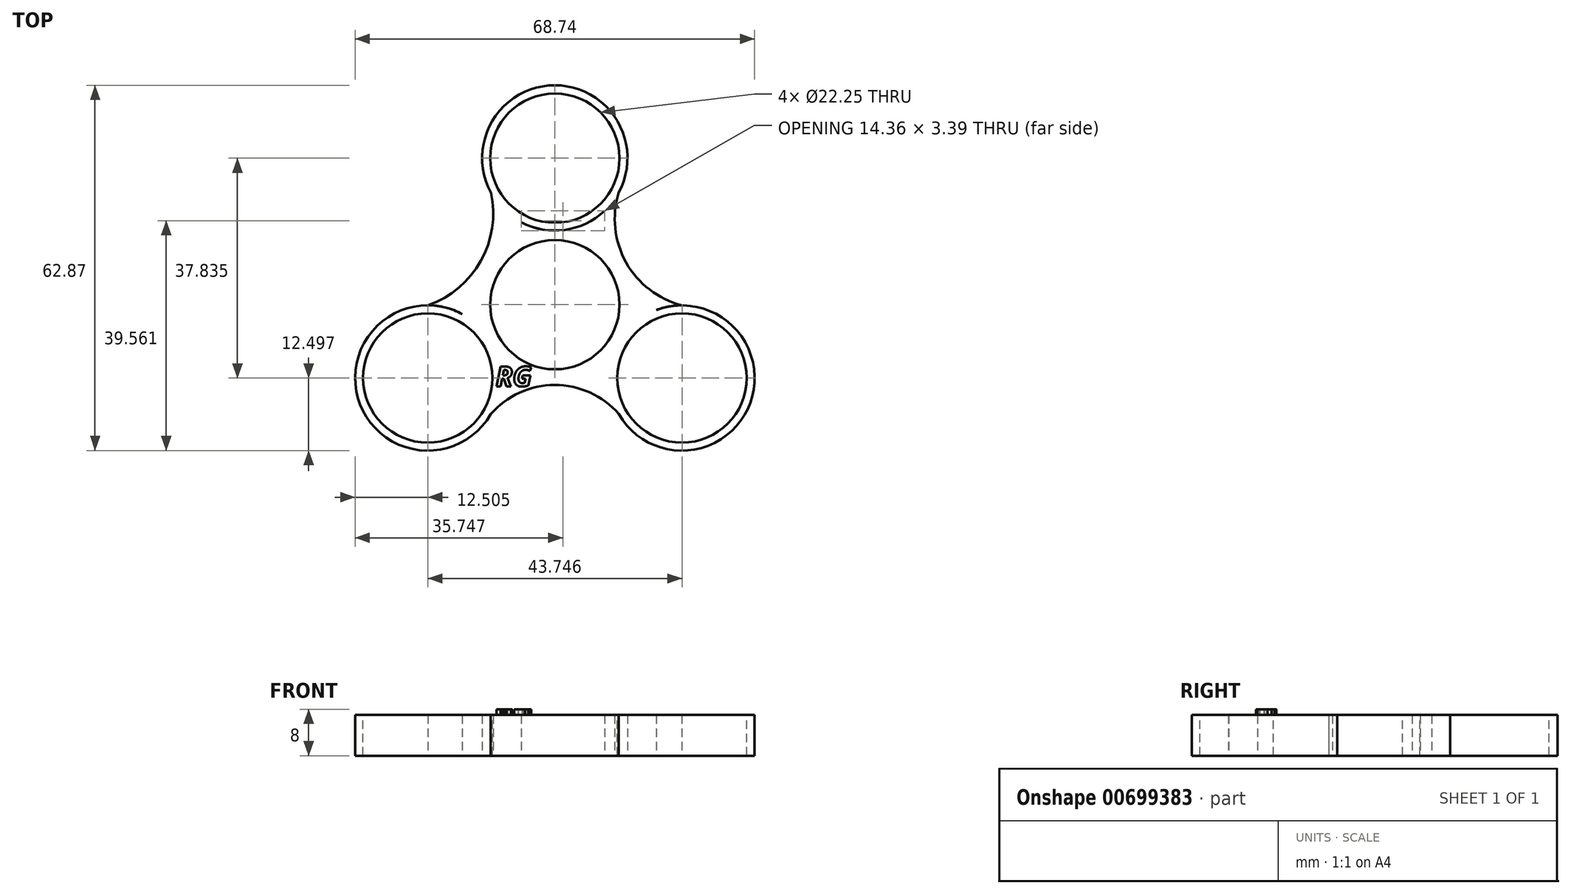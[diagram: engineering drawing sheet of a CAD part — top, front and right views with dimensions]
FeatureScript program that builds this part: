
annotation { "Feature Type Name" : "Feature", "Feature Type Description" : "" }
export const myFeature = defineFeature(function(context is Context, id is Id, definition is map)
    precondition{}
    {
        {
            var Q0;
            Q0=qCreatedBy(makeId("Top.planeOp"),FACE);
            var sketch = newSketch(context, id + "F0", { "sketchPlane" : qUnion([Q0])});
            skCircle(sketch, "E0", {"center": v(0, 0) * mm, "radius": 11.12 * mm});
            skCircle(sketch, "E1", {"center": v(0, 25.25) * mm, "radius": 11.12 * mm});
            skCircle(sketch, "E2", {"center": v(-21.87, -12.62) * mm, "radius": 11.12 * mm});
            skCircle(sketch, "E3", {"center": v(21.87, -12.62) * mm, "radius": 11.12 * mm});
            skSolve(sketch);
        }
        {
            var Q0;
            Q0=qCreatedBy(makeId("Top.planeOp"),FACE);
            var sketch = newSketch(context, id + "F1", { "sketchPlane" : qUnion([Q0])});
            skCircle(sketch, "E4", {"center": v(-21.87, -12.62) * mm, "radius": 12.5 * mm});
            skCircle(sketch, "E5", {"center": v(21.87, -12.62) * mm, "radius": 12.5 * mm});
            skCircle(sketch, "E6", {"center": v(0, 25.25) * mm, "radius": 12.5 * mm});
            skSolve(sketch);
        }
        {
            var Q0;
            Q0=qCreatedBy(makeId("Top.planeOp"),FACE);
            var sketch = newSketch(context, id + "F2", { "sketchPlane" : qUnion([Q0])});
            skArc(sketch, "E7", {"start": v(-21.85, -0.1) * mm, "mid": v(-12.72, 7.56) * mm, "end": v(-11, 19.35) * mm});
            skArc(sketch, "E8", {"start": v(11, 19.33) * mm, "mid": v(12.26, 7.28) * mm, "end": v(21.85, -0.12) * mm});
            skArc(sketch, "E9", {"start": v(11.03, -18.84) * mm, "mid": v(-0.01, -13.83) * mm, "end": v(-11.04, -18.87) * mm});
            skArc(sketch, "E10", {"start": v(-11, 19.35) * mm, "mid": v(0, 12.74) * mm, "end": v(11, 19.33) * mm});
            skArc(sketch, "E11", {"start": v(21.85, -0.12) * mm, "mid": v(11.06, -6.37) * mm, "end": v(11.03, -18.84) * mm});
            skArc(sketch, "E12", {"start": v(-11.04, -18.87) * mm, "mid": v(-11.05, -6.38) * mm, "end": v(-21.85, -0.1) * mm});
            skSolve(sketch);
        }
        {
            var Q0;
            Q0 = qSketchRegion(id + "F2", true);
            extrude(context, id + "F3", {"entities" : qUnion([Q0]), "depth" : 7 * mm, "offsetDistance" : 25 * mm});
        }
        {
            var Q0;
            Q0 = qSketchRegion(id + "F1", true);
            extrude(context, id + "F4", {"entities" : qUnion([Q0]), "operationType" : NewBodyOperationType.ADD, "depth" : 7 * mm, "offsetDistance" : 25 * mm});
        }
        {
            var Q0;
            Q0 = qSketchRegion(id + "F0", true);
            extrude(context, id + "F5", {"entities" : qUnion([Q0]), "operationType" : NewBodyOperationType.REMOVE, "oppositeDirection" : true, "depth" : 25 * mm, "offsetDistance" : 25 * mm});
        }
        {
            var Q0;
            Q0 = qSketchRegion(id + "F0", true);
            extrude(context, id + "F6", {"entities" : qUnion([Q0]), "operationType" : NewBodyOperationType.REMOVE, "oppositeDirection" : true, "depth" : 25 * mm, "offsetDistance" : 25 * mm});
        }
        {
            var Q0;
            Q0=makeQuery(id+"F4.boolean.opBoolean","MERGE",FACE,{"derivedFrom":[makeQuery(id+"F3.opExtrude","CAP_FACE",FACE,{"disambiguationData":[OSD([sQuery(id+"F2.wireOp",EDGE,"E7"),sQuery(id+"F2.wireOp",EDGE,"E8"),sQuery(id+"F2.wireOp",EDGE,"E9"),sQuery(id+"F2.wireOp",EDGE,"E10"),sQuery(id+"F2.wireOp",EDGE,"E11"),sQuery(id+"F2.wireOp",EDGE,"E12")])],"isStart":false}),makeQuery(id+"F4.opExtrude","CAP_FACE",FACE,{"disambiguationData":[OSD([sQuery(id+"F1.wireOp",EDGE,"E4")])],"isStart":false}),makeQuery(id+"F4.opExtrude","CAP_FACE",FACE,{"disambiguationData":[OSD([sQuery(id+"F1.wireOp",EDGE,"E5")])],"isStart":false}),makeQuery(id+"F4.opExtrude","CAP_FACE",FACE,{"disambiguationData":[OSD([sQuery(id+"F1.wireOp",EDGE,"E6")])],"isStart":false})]});
            var sketch = newSketch(context, id + "F7", { "sketchPlane" : qUnion([Q0])});
            skCircle(sketch, "E13", {"center": v(0, 25.21) * mm, "radius": 11.12 * mm});
            skSolve(sketch);
        }
        {
            var Q0;
            Q0 = qSketchRegion(id + "F7", true);
            extrude(context, id + "F8", {"entities" : qUnion([Q0]), "operationType" : NewBodyOperationType.REMOVE, "oppositeDirection" : true, "depth" : 25 * mm, "offsetDistance" : 25 * mm});
        }
        {
            var Q0;
            Q0=makeQuery(id+"F4.boolean.opBoolean","MERGE",FACE,{"derivedFrom":[makeQuery(id+"F3.opExtrude","CAP_FACE",FACE,{"disambiguationData":[OSD([sQuery(id+"F2.wireOp",EDGE,"E7"),sQuery(id+"F2.wireOp",EDGE,"E8"),sQuery(id+"F2.wireOp",EDGE,"E9"),sQuery(id+"F2.wireOp",EDGE,"E10"),sQuery(id+"F2.wireOp",EDGE,"E11"),sQuery(id+"F2.wireOp",EDGE,"E12")])],"isStart":false}),makeQuery(id+"F4.opExtrude","CAP_FACE",FACE,{"disambiguationData":[OSD([sQuery(id+"F1.wireOp",EDGE,"E4")])],"isStart":false}),makeQuery(id+"F4.opExtrude","CAP_FACE",FACE,{"disambiguationData":[OSD([sQuery(id+"F1.wireOp",EDGE,"E5")])],"isStart":false}),makeQuery(id+"F4.opExtrude","CAP_FACE",FACE,{"disambiguationData":[OSD([sQuery(id+"F1.wireOp",EDGE,"E6")])],"isStart":false})]});
            var sketch = newSketch(context, id + "F9", { "sketchPlane" : qUnion([Q0])});
            skCircle(sketch, "E14", {"center": v(0, 0) * mm, "radius": 11.12 * mm});
            skSolve(sketch);
        }
        {
            var Q0;
            Q0 = qSketchRegion(id + "F9", true);
            extrude(context, id + "F10", {"entities" : qUnion([Q0]), "operationType" : NewBodyOperationType.REMOVE, "oppositeDirection" : true, "depth" : 25 * mm, "offsetDistance" : 25 * mm});
        }
        {
            var Q0;
            Q0=makeQuery(id+"F4.boolean.opBoolean","MERGE",FACE,{"derivedFrom":[makeQuery(id+"F3.opExtrude","CAP_FACE",FACE,{"disambiguationData":[OSD([sQuery(id+"F2.wireOp",EDGE,"E7"),sQuery(id+"F2.wireOp",EDGE,"E8"),sQuery(id+"F2.wireOp",EDGE,"E9"),sQuery(id+"F2.wireOp",EDGE,"E10"),sQuery(id+"F2.wireOp",EDGE,"E11"),sQuery(id+"F2.wireOp",EDGE,"E12")])],"isStart":false}),makeQuery(id+"F4.opExtrude","CAP_FACE",FACE,{"disambiguationData":[OSD([sQuery(id+"F1.wireOp",EDGE,"E4")])],"isStart":false}),makeQuery(id+"F4.opExtrude","CAP_FACE",FACE,{"disambiguationData":[OSD([sQuery(id+"F1.wireOp",EDGE,"E5")])],"isStart":false}),makeQuery(id+"F4.opExtrude","CAP_FACE",FACE,{"disambiguationData":[OSD([sQuery(id+"F1.wireOp",EDGE,"E6")])],"isStart":false})]});
            var sketch = newSketch(context, id + "F11", { "sketchPlane" : qUnion([Q0])});
            skCircle(sketch, "E15", {"center": v(-21.87, -12.62) * mm, "radius": 11.12 * mm});
            skSolve(sketch);
        }
        {
            var Q0;
            Q0 = qSketchRegion(id + "F11", true);
            extrude(context, id + "F12", {"entities" : qUnion([Q0]), "operationType" : NewBodyOperationType.REMOVE, "oppositeDirection" : true, "depth" : 25 * mm, "offsetDistance" : 25 * mm});
        }
        {
            var Q0;
            Q0=makeQuery(id+"F4.boolean.opBoolean","MERGE",FACE,{"derivedFrom":[makeQuery(id+"F3.opExtrude","CAP_FACE",FACE,{"disambiguationData":[OSD([sQuery(id+"F2.wireOp",EDGE,"E7"),sQuery(id+"F2.wireOp",EDGE,"E8"),sQuery(id+"F2.wireOp",EDGE,"E9"),sQuery(id+"F2.wireOp",EDGE,"E10"),sQuery(id+"F2.wireOp",EDGE,"E11"),sQuery(id+"F2.wireOp",EDGE,"E12")])],"isStart":false}),makeQuery(id+"F4.opExtrude","CAP_FACE",FACE,{"disambiguationData":[OSD([sQuery(id+"F1.wireOp",EDGE,"E4")])],"isStart":false}),makeQuery(id+"F4.opExtrude","CAP_FACE",FACE,{"disambiguationData":[OSD([sQuery(id+"F1.wireOp",EDGE,"E5")])],"isStart":false}),makeQuery(id+"F4.opExtrude","CAP_FACE",FACE,{"disambiguationData":[OSD([sQuery(id+"F1.wireOp",EDGE,"E6")])],"isStart":false})]});
            var sketch = newSketch(context, id + "F13", { "sketchPlane" : qUnion([Q0])});
            skCircle(sketch, "E16", {"center": v(21.88, -12.62) * mm, "radius": 11.12 * mm});
            skSolve(sketch);
        }
        {
            var Q0;
            Q0 = qSketchRegion(id + "F13", true);
            extrude(context, id + "F14", {"entities" : qUnion([Q0]), "operationType" : NewBodyOperationType.REMOVE, "oppositeDirection" : true, "depth" : 25 * mm, "offsetDistance" : 25 * mm});
        }
        {
            var Q0;
            Q0=makeQuery(id+"F4.boolean.opBoolean","MERGE",FACE,{"derivedFrom":[makeQuery(id+"F3.opExtrude","CAP_FACE",FACE,{"disambiguationData":[OSD([sQuery(id+"F2.wireOp",EDGE,"E7"),sQuery(id+"F2.wireOp",EDGE,"E8"),sQuery(id+"F2.wireOp",EDGE,"E9"),sQuery(id+"F2.wireOp",EDGE,"E10"),sQuery(id+"F2.wireOp",EDGE,"E11"),sQuery(id+"F2.wireOp",EDGE,"E12")])],"isStart":false}),makeQuery(id+"F4.opExtrude","CAP_FACE",FACE,{"disambiguationData":[OSD([sQuery(id+"F1.wireOp",EDGE,"E4")])],"isStart":false}),makeQuery(id+"F4.opExtrude","CAP_FACE",FACE,{"disambiguationData":[OSD([sQuery(id+"F1.wireOp",EDGE,"E5")])],"isStart":false}),makeQuery(id+"F4.opExtrude","CAP_FACE",FACE,{"disambiguationData":[OSD([sQuery(id+"F1.wireOp",EDGE,"E6")])],"isStart":false})]});
            var sketch = newSketch(context, id + "F15", { "sketchPlane" : qUnion([Q0])});
            skText(sketch, "E17", { "text": "RG", "fontName": "OpenSans-BoldItalic.ttf"});
            const initialGuessF15  = {"E17": [-0.01017, -0.01406, 1, 0, 0.00343]};
            skSetInitialGuess(sketch, initialGuessF15);
            skSolve(sketch);
        }
        {
            var Q0;
            Q0 = qSketchRegion(id + "F15", true);
            extrude(context, id + "F16", {"entities" : qUnion([Q0]), "operationType" : NewBodyOperationType.ADD, "depth" : 1 * mm, "offsetDistance" : 25 * mm});
        }
    });
